# Revit family: Roof-Accessories_Menzies-Metal_Roof_Anchor_Flashing (1)
name_source: partatom
category: Specialty Equipment
revit_build: Autodesk Revit 2018 (Build: 20170223_1515(x64)
units: mm (PartAtom-declared; Revit-internal decimal feet)

## family parameters
Cut with Voids When Loaded = No
Host = Face
OmniClass Number = 23.70.50.21.24.11
OmniClass Title = Roof Waste Water Drains
Part Type = Normal
Room Calculation Point = No
Round Connector Dimension = Use Diameter
Shared = No

## types (5) — shared parameters
Assembly Code = D2040200
CW Connection = No
Default Elevation = 48 "
Description = Roof Anchor Flashing
Drain Flow = 0 GPM
Edition number = 1
HW Connection = No
Manufacturer = Menzies Metal Products
Model = 400-4400
Pipe Length = 8 "
Pipe diameter = 12 "
Product Guid = 3faf9270-de75-475c-b816-8947cb374fa5
Product Material = Metal - Menzies Metal Products - Stainless Steel
Product data url = https://www.bimobject.com
URL = https://www.menzies-metal.com
Vent Connection = No
Waste Connection = No
Weight = 5.90 lbf

## per-type parameters (varying)
| type | Size |
| 3" | 3 " |
| 4" | 2 " |
| 1 1/4" | 4 " |
| 1 1/2" | 3 " |
| 2" | 3 " |

## geometry (parser evidence)
native form markers: Sweep x1
no freeform markers — native parametric forms only
